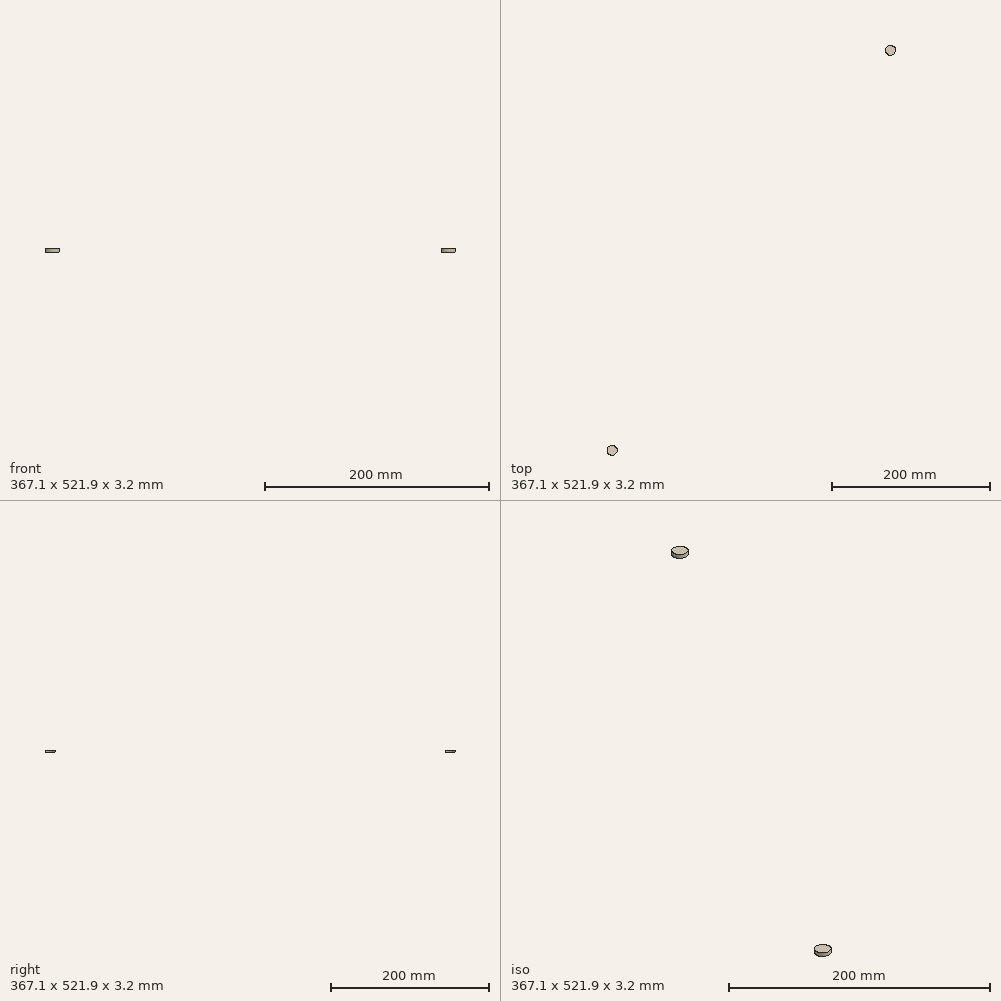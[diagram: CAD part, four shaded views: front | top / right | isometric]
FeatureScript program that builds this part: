
annotation { "Feature Type Name" : "Feature", "Feature Type Description" : "" }
export const myFeature = defineFeature(function(context is Context, id is Id, definition is map)
    precondition{}
    {
        {
            var Q0;
            Q0=qCreatedBy(makeId("Top.planeOp"),FACE);
            var sketch = newSketch(context, id + "F0", { "sketchPlane" : qUnion([Q0])});
            skLineSegment(sketch, "E0.bottom", {"start": v(209.55, 285.75) * mm, "end": v(-209.55, 285.75) * mm});
            skLineSegment(sketch, "E0.top", {"start": v(209.55, -285.75) * mm, "end": v(-209.55, -285.75) * mm});
            skLineSegment(sketch, "E0.left", {"start": v(209.55, 285.75) * mm, "end": v(209.55, -285.75) * mm});
            skLineSegment(sketch, "E0.right", {"start": v(-209.55, 285.75) * mm, "end": v(-209.55, -285.75) * mm});
            skPoint(sketch, "E0.middle", {"position": v(0, 0) * mm});
            skSolve(sketch);
        }
        {
            var Q0;
            Q0 = qSketchRegion(id + "F0", true);
            extrude(context, id + "F1", {"entities" : qUnion([Q0]), "depth" : 3.17 * mm});
        }
        {
            var Q0;
            Q0=makeQuery(id+"F1.opExtrude","CAP_FACE",FACE,{"disambiguationData":[OSD([sQuery(id+"F0.wireOp",EDGE,"E0.bottom"),sQuery(id+"F0.wireOp",EDGE,"E0.top"),sQuery(id+"F0.wireOp",EDGE,"E0.left"),sQuery(id+"F0.wireOp",EDGE,"E0.right")])],"isStart":false});
            var sketch = newSketch(context, id + "F2", { "sketchPlane" : qUnion([Q0])});
            skLineSegment(sketch, "E1", {"start": v(0, 285.75) * mm, "end": v(0, -285.75) * mm, "construction": true});
            skLineSegment(sketch, "E2", {"start": v(-209.55, 0) * mm, "end": v(209.55, 0) * mm, "construction": true});
            skCircle(sketch, "E3", {"center": v(-177.18, 254.58) * mm, "radius": 6.35 * mm});
            skCircle(sketch, "E4.MirrorC", {"center": v(-177.18, -254.58) * mm, "radius": 6.35 * mm});
            skCircle(sketch, "E5.MirrorC", {"center": v(177.18, 254.58) * mm, "radius": 6.35 * mm});
            skCircle(sketch, "E6.MirrorC", {"center": v(177.18, -254.58) * mm, "radius": 6.35 * mm});
            skSolve(sketch);
        }
        {
            var Q0;
            Q0=makeQuery(id+"F2.imprint","IMPRINT",FACE,{"disambiguationData":[TD([[makeQuery(id+"F2.imprint","IMPRINT",EDGE,{"derivedFrom":sQuery(id+"F2.wireOp",EDGE,"E3")}),1.0]])]});
            var Q1;
            Q1=makeQuery(id+"F2.imprint","IMPRINT",FACE,{"disambiguationData":[TD([[makeQuery(id+"F2.imprint","IMPRINT",EDGE,{"derivedFrom":sQuery(id+"F2.wireOp",EDGE,"E5.MirrorC")}),-1.0]])]});
            var Q2;
            Q2=makeQuery(id+"F2.imprint","IMPRINT",FACE,{"disambiguationData":[TD([[makeQuery(id+"F2.imprint","IMPRINT",EDGE,{"derivedFrom":sQuery(id+"F2.wireOp",EDGE,"E6.MirrorC")}),1.0]])]});
            var Q3;
            Q3=makeQuery(id+"F2.imprint","IMPRINT",FACE,{"disambiguationData":[TD([[makeQuery(id+"F2.imprint","IMPRINT",EDGE,{"derivedFrom":sQuery(id+"F2.wireOp",EDGE,"E4.MirrorC")}),-1.0]])]});
            extrude(context, id + "F3", {"entities" : qUnion([Q0, Q1, Q2, Q3]), "operationType" : NewBodyOperationType.REMOVE, "oppositeDirection" : true, "depth" : 25.4 * mm});
        }
    });
